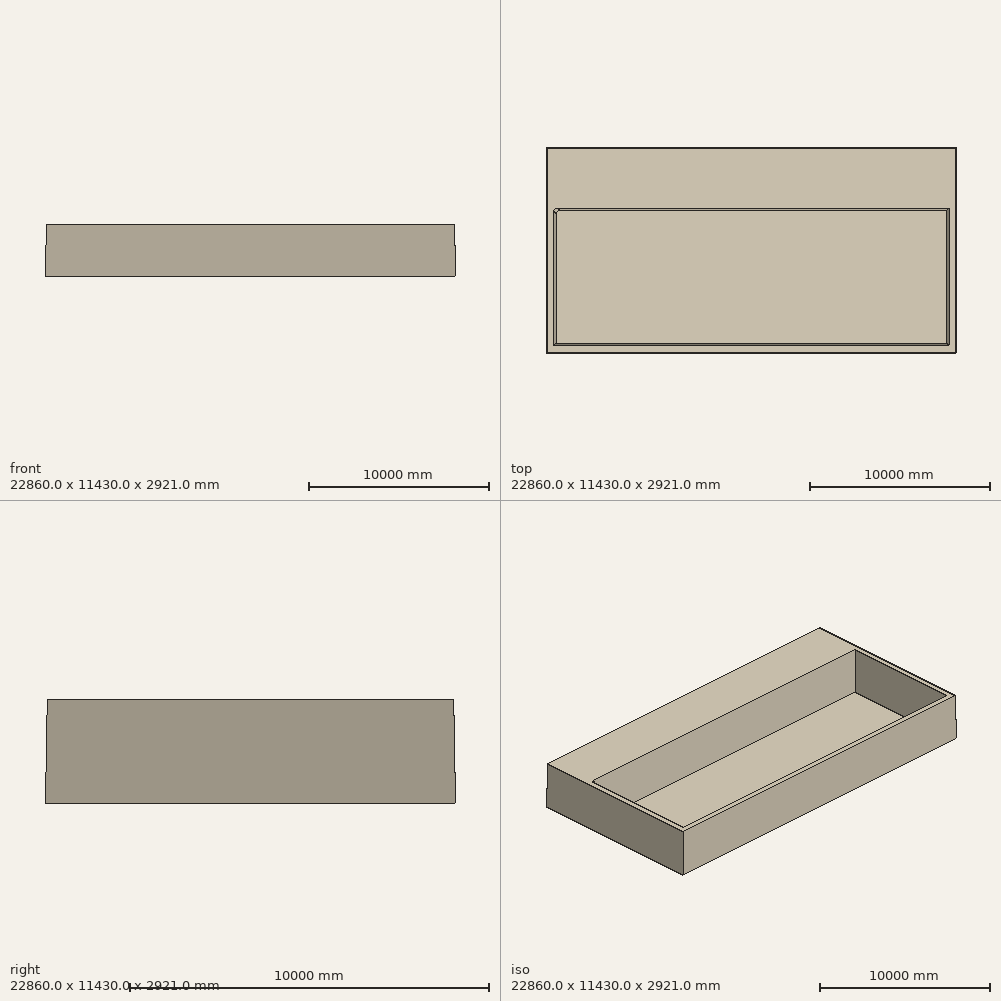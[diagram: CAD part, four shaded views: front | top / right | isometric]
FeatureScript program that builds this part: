
annotation { "Feature Type Name" : "Feature", "Feature Type Description" : "" }
export const myFeature = defineFeature(function(context is Context, id is Id, definition is map)
    precondition{}
    {
        {
            var Q0;
            Q0=qCreatedBy(makeId("Top.planeOp"),FACE);
            var sketch = newSketch(context, id + "F0", { "sketchPlane" : qUnion([Q0])});
            skLineSegment(sketch, "E0.bottom", {"start": v(-8450.68, -5729.86) * mm, "end": v(14409.32, -5729.86) * mm});
            skLineSegment(sketch, "E0.top", {"start": v(-8450.68, 5700.14) * mm, "end": v(14409.32, 5700.14) * mm});
            skLineSegment(sketch, "E0.left", {"start": v(-8450.68, -5729.86) * mm, "end": v(-8450.68, 5700.14) * mm});
            skLineSegment(sketch, "E0.right", {"start": v(14409.32, -5729.86) * mm, "end": v(14409.32, 5700.14) * mm});
            skSolve(sketch);
        }
        {
            var Q0;
            Q0=makeQuery(id+"F0.imprint","IMPRINT",FACE,{"disambiguationData":[TD([[makeQuery(id+"F0.imprint","IMPRINT",EDGE,{"derivedFrom":sQuery(id+"F0.wireOp",EDGE,"E0.bottom")}),1.0]])]});
            extrude(context, id + "F1", {"entities" : qUnion([Q0]), "depth" : 2921 * mm, "hasDraft" : true, "draftAngle" : 1 * degree, "draftPullDirection" : true});
        }
        {
            var Q0;
            Q0=makeQuery(id+"F1.opExtrude","CAP_FACE",FACE,{"disambiguationData":[OSD([sQuery(id+"F0.wireOp",EDGE,"E0.bottom"),sQuery(id+"F0.wireOp",EDGE,"E0.top"),sQuery(id+"F0.wireOp",EDGE,"E0.left"),sQuery(id+"F0.wireOp",EDGE,"E0.right")])],"isStart":false});
            var sketch = newSketch(context, id + "F2", { "sketchPlane" : qUnion([Q0])});
            skLineSegment(sketch, "E1.bottom", {"start": v(-8044.1, -5323.27) * mm, "end": v(14002.73, -5323.27) * mm});
            skLineSegment(sketch, "E1.top", {"start": v(-8044.1, 2347.16) * mm, "end": v(14002.73, 2347.16) * mm});
            skLineSegment(sketch, "E1.left", {"start": v(-8044.1, -5323.27) * mm, "end": v(-8044.1, 2347.16) * mm});
            skLineSegment(sketch, "E1.right", {"start": v(14002.73, -5323.27) * mm, "end": v(14002.73, 2347.16) * mm});
            skSolve(sketch);
        }
        {
            var Q0;
            Q0 = qSketchRegion(id + "F2", true);
            extrude(context, id + "F3", {"entities" : qUnion([Q0]), "operationType" : NewBodyOperationType.REMOVE, "oppositeDirection" : true, "depth" : 2794 * mm, "hasDraft" : true, "draftAngle" : 3 * degree, "draftPullDirection" : true});
        }
        {
            var Q0;
            Q0=makeQuery(id+"F1.opExtrude","CAP_FACE",FACE,{"disambiguationData":[OSD([sQuery(id+"F0.wireOp",EDGE,"E0.bottom"),sQuery(id+"F0.wireOp",EDGE,"E0.top"),sQuery(id+"F0.wireOp",EDGE,"E0.left"),sQuery(id+"F0.wireOp",EDGE,"E0.right")])],"isStart":true});
            shell(context, id + "F4", {"entities" : qUnion([Q0]), "thickness" : 25.4 * mm});
        }
        {
            var Q0;
            Q0=makeQuery(id+"F3.boolean.opBoolean","COPY",EDGE,{"derivedFrom":makeQuery(id+"F3.opExtrude","SWEPT_EDGE",EDGE,{"disambiguationData":[OSD([sQuery(id+"F2.wireOp",EDGE,"E1.top"),sQuery(id+"F2.wireOp",EDGE,"E1.left")])]})});
            fillet(context, id + "F5", {"entities" : qUnion([Q0]), "radius" : 203.2 * mm, "tangentPropagation" : true, "allowEdgeOverflow" : false});
        }
    });
